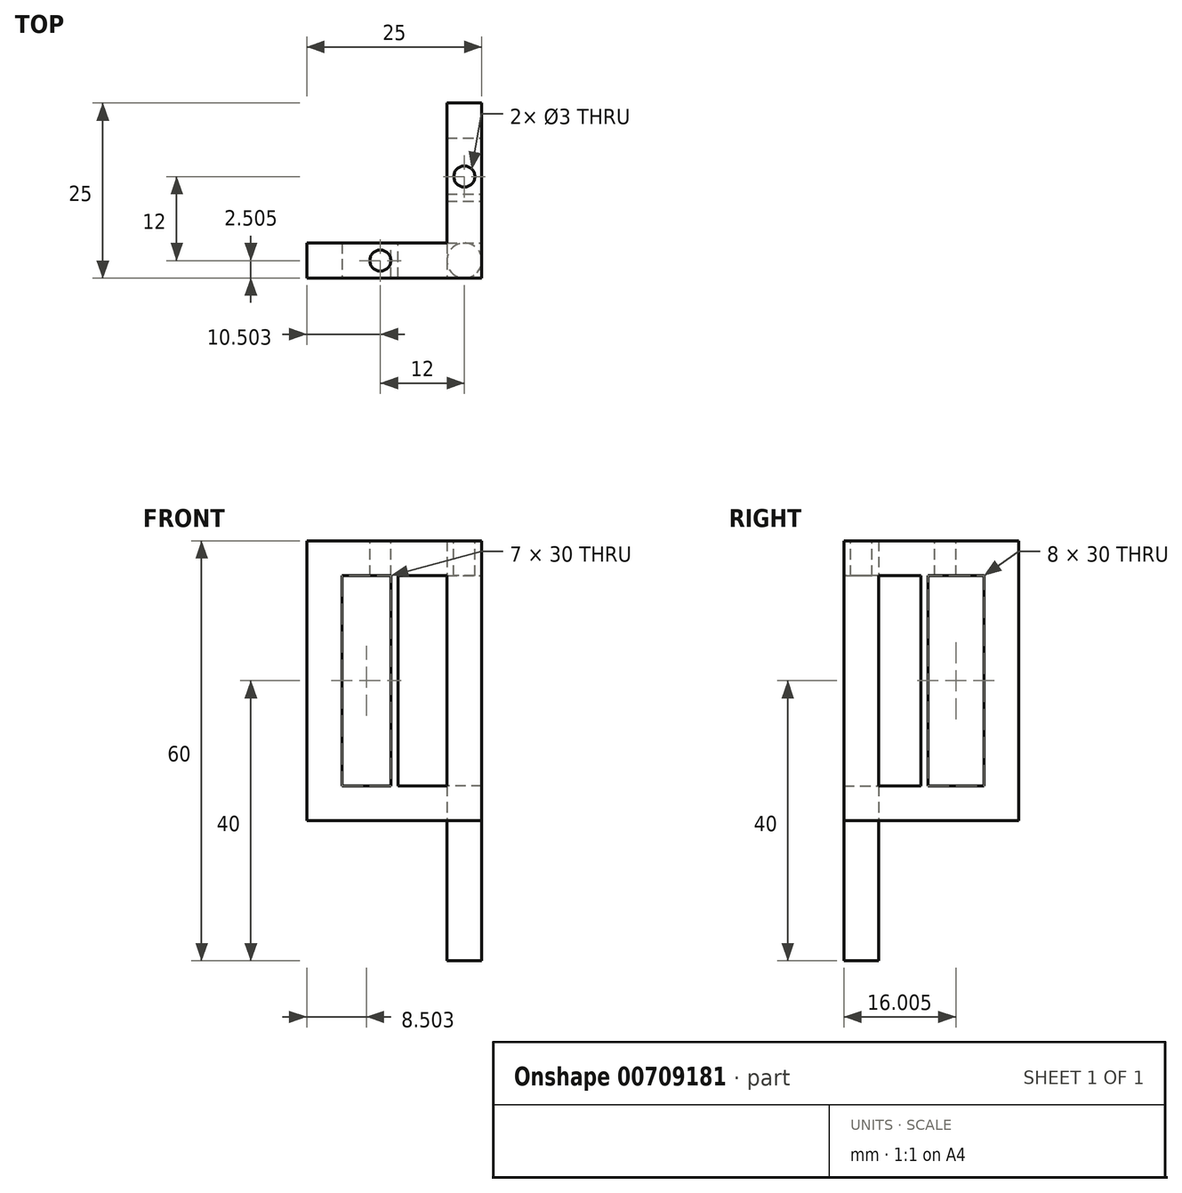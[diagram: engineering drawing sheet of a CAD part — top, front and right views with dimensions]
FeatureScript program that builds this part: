
annotation { "Feature Type Name" : "Feature", "Feature Type Description" : "" }
export const myFeature = defineFeature(function(context is Context, id is Id, definition is map)
    precondition{}
    {
        {
            var Q0;
            Q0=qCreatedBy(makeId("Top.planeOp"),FACE);
            var sketch = newSketch(context, id + "F0", { "sketchPlane" : qUnion([Q0])});
            skLineSegment(sketch, "E0.top", {"start": v(-54.93, 13.4) * mm, "end": v(-29.93, 13.4) * mm});
            skLineSegment(sketch, "E0.right", {"start": v(-29.93, 38.4) * mm, "end": v(-29.93, 13.4) * mm});
            skLineSegment(sketch, "E1.top", {"start": v(-54.93, 18.4) * mm, "end": v(-34.93, 18.4) * mm});
            skLineSegment(sketch, "E1.right", {"start": v(-34.93, 38.4) * mm, "end": v(-34.93, 18.4) * mm});
            skLineSegment(sketch, "E2", {"start": v(-49.93, 18.4) * mm, "end": v(-49.93, 13.4) * mm});
            skLineSegment(sketch, "E3", {"start": v(-34.93, 33.4) * mm, "end": v(-29.93, 33.4) * mm});
            skPoint(sketch, "E4", {"position": v(-32.43, 15.9) * mm});
            skCircle(sketch, "E5", {"center": v(-32.43, 15.9) * mm, "radius": 2.5 * mm});
            skLineSegment(sketch, "E6.bottom", {"start": v(-34.93, 18.4) * mm, "end": v(-29.93, 18.4) * mm});
            skLineSegment(sketch, "E6.top", {"start": v(-34.93, 13.4) * mm, "end": v(-29.93, 13.4) * mm});
            skLineSegment(sketch, "E6.left", {"start": v(-34.93, 18.4) * mm, "end": v(-34.93, 13.4) * mm});
            skLineSegment(sketch, "E6.right", {"start": v(-29.93, 18.4) * mm, "end": v(-29.93, 13.4) * mm});
            skLineSegment(sketch, "E7", {"start": v(-34.93, 38.4) * mm, "end": v(-29.93, 38.4) * mm});
            skLineSegment(sketch, "E8", {"start": v(-54.93, 18.4) * mm, "end": v(-54.93, 13.4) * mm});
            skLineSegment(sketch, "E9.bottom", {"start": v(-34.93, 24.4) * mm, "end": v(-29.93, 24.4) * mm});
            skLineSegment(sketch, "E9.top", {"start": v(-34.93, 25.4) * mm, "end": v(-29.93, 25.4) * mm});
            skLineSegment(sketch, "E9.left", {"start": v(-34.93, 24.4) * mm, "end": v(-34.93, 25.4) * mm});
            skLineSegment(sketch, "E9.right", {"start": v(-29.93, 24.4) * mm, "end": v(-29.93, 25.4) * mm});
            skLineSegment(sketch, "E10.bottom", {"start": v(-42.93, 13.4) * mm, "end": v(-41.93, 13.4) * mm});
            skLineSegment(sketch, "E10.top", {"start": v(-42.93, 18.4) * mm, "end": v(-41.93, 18.4) * mm});
            skLineSegment(sketch, "E10.left", {"start": v(-41.93, 13.4) * mm, "end": v(-41.93, 18.4) * mm});
            skLineSegment(sketch, "E10.right", {"start": v(-42.93, 13.4) * mm, "end": v(-42.93, 18.4) * mm});
            skSolve(sketch);
        }
        {
            var Q0;
            {var subQ0=sQuery(id+"F0.wireOp",EDGE,"E3");Q0=makeQuery(id+"F0.imprint","IMPRINT",FACE,{"disambiguationData":[TD([[makeQuery(id+"F0.imprint","IMPRINT",EDGE,{"derivedFrom":subQ0}),-1.0]])]});}
            var Q1;
            {var subQ0=sQuery(id+"F0.wireOp",EDGE,"E2");Q1=makeQuery(id+"F0.imprint","IMPRINT",FACE,{"disambiguationData":[TD([[makeQuery(id+"F0.imprint","IMPRINT",EDGE,{"derivedFrom":subQ0}),1.0]])]});}
            var Q2;
            {var subQ0=sQuery(id+"F0.wireOp",EDGE,"E2");Q2=makeQuery(id+"F0.imprint","IMPRINT",FACE,{"disambiguationData":[TD([[makeQuery(id+"F0.imprint","IMPRINT",EDGE,{"derivedFrom":subQ0}),-1.0]])]});}
            var Q3;
            {var subQ0=sQuery(id+"F0.wireOp",EDGE,"E3");Q3=makeQuery(id+"F0.imprint","IMPRINT",FACE,{"disambiguationData":[TD([[makeQuery(id+"F0.imprint","IMPRINT",EDGE,{"derivedFrom":subQ0}),1.0]])]});}
            var Q4;
            {var subQ0=sQuery(id+"F0.wireOp",EDGE,"E5");var subQ1=makeQuery(id+"F0.imprint","INTERSECT",VERTEX,{"derivedFrom":[subQ0,sQuery(id+"F0.wireOp",EDGE,"E6.bottom")]});Q4=makeQuery(id+"F0.imprint","IMPRINT",FACE,{"disambiguationData":[TD([[makeQuery(id+"F0.imprint","IMPRINT",EDGE,{"disambiguationData":[TD([[subQ1,1.0]])],"derivedFrom":subQ0}),1.0]])]});}
            var Q5;
            {var subQ0=sQuery(id+"F0.wireOp",EDGE,"E6.bottom");var subQ1=sQuery(id+"F0.wireOp",EDGE,"E0.right");var subQ2=makeQuery(id+"F0.imprint","INTERSECT",VERTEX,{"derivedFrom":[subQ1,subQ0]});Q5=makeQuery(id+"F0.imprint","IMPRINT",FACE,{"disambiguationData":[TD([[makeQuery(id+"F0.imprint","IMPRINT",EDGE,{"disambiguationData":[TD([[subQ2,-1.0]])],"derivedFrom":subQ1}),-1.0]])]});}
            var Q6;
            {var subQ0=sQuery(id+"F0.wireOp",EDGE,"E6.left");var subQ1=sQuery(id+"F0.wireOp",EDGE,"E0.top");var subQ2=makeQuery(id+"F0.imprint","INTERSECT",VERTEX,{"derivedFrom":[subQ1,subQ0]});Q6=makeQuery(id+"F0.imprint","IMPRINT",FACE,{"disambiguationData":[TD([[makeQuery(id+"F0.imprint","IMPRINT",EDGE,{"disambiguationData":[TD([[subQ2,-1.0]])],"derivedFrom":subQ1}),1.0]])]});}
            var Q7;
            {var subQ0=sQuery(id+"F0.wireOp",EDGE,"E0.right");var subQ1=sQuery(id+"F0.wireOp",EDGE,"E0.top");var subQ2=makeQuery(id+"F0.imprint","INTERSECT",VERTEX,{"derivedFrom":[subQ1,subQ0]});Q7=makeQuery(id+"F0.imprint","IMPRINT",FACE,{"disambiguationData":[TD([[makeQuery(id+"F0.imprint","IMPRINT",EDGE,{"disambiguationData":[TD([[subQ2,1.0]])],"derivedFrom":subQ1}),1.0]])]});}
            var Q8;
            {var subQ0=sQuery(id+"F0.wireOp",EDGE,"E6.bottom");var subQ1=sQuery(id+"F0.wireOp",EDGE,"E5");var subQ2=makeQuery(id+"F0.imprint","INTERSECT",VERTEX,{"derivedFrom":[subQ1,subQ0]});Q8=makeQuery(id+"F0.imprint","IMPRINT",FACE,{"disambiguationData":[TD([[makeQuery(id+"F0.imprint","IMPRINT",EDGE,{"disambiguationData":[TD([[subQ2,-1.0]])],"derivedFrom":subQ1}),-1.0]])]});}
            var Q9;
            {var subQ6=sQuery(id+"F0.wireOp",EDGE,"E10.left");Q9=makeQuery(id+"F0.imprint","IMPRINT",FACE,{"disambiguationData":[TD([[makeQuery(id+"F0.imprint","IMPRINT",EDGE,{"derivedFrom":subQ6}),-1.0]])]});}
            var Q10;
            {var subQ0=sQuery(id+"F0.wireOp",EDGE,"E10.left");Q10=makeQuery(id+"F0.imprint","IMPRINT",FACE,{"disambiguationData":[TD([[makeQuery(id+"F0.imprint","IMPRINT",EDGE,{"derivedFrom":subQ0}),1.0]])]});}
            var Q11;
            {var subQ6=sQuery(id+"F0.wireOp",EDGE,"E9.bottom");Q11=makeQuery(id+"F0.imprint","IMPRINT",FACE,{"disambiguationData":[TD([[makeQuery(id+"F0.imprint","IMPRINT",EDGE,{"derivedFrom":subQ6}),-1.0]])]});}
            var Q12;
            {var subQ0=sQuery(id+"F0.wireOp",EDGE,"E9.bottom");Q12=makeQuery(id+"F0.imprint","IMPRINT",FACE,{"disambiguationData":[TD([[makeQuery(id+"F0.imprint","IMPRINT",EDGE,{"derivedFrom":subQ0}),1.0]])]});}
            extrude(context, id + "F1", {"entities" : qUnion([Q0, Q1, Q2, Q3, Q4, Q5, Q6, Q7, Q8, Q9, Q10, Q11, Q12]), "depth" : 5 * mm, "offsetDistance" : 25 * mm});
        }
        {
            var Q0;
            {var subQ0=sQuery(id+"F0.wireOp",EDGE,"E2");Q0=makeQuery(id+"F0.imprint","IMPRINT",FACE,{"disambiguationData":[TD([[makeQuery(id+"F0.imprint","IMPRINT",EDGE,{"derivedFrom":subQ0}),-1.0]])]});}
            var Q1;
            {var subQ0=sQuery(id+"F0.wireOp",EDGE,"E6.bottom");var subQ1=sQuery(id+"F0.wireOp",EDGE,"E5");var subQ2=makeQuery(id+"F0.imprint","INTERSECT",VERTEX,{"derivedFrom":[subQ1,subQ0]});Q1=makeQuery(id+"F0.imprint","IMPRINT",FACE,{"disambiguationData":[TD([[makeQuery(id+"F0.imprint","IMPRINT",EDGE,{"disambiguationData":[TD([[subQ2,-1.0]])],"derivedFrom":subQ1}),-1.0]])]});}
            var Q2;
            {var subQ0=sQuery(id+"F0.wireOp",EDGE,"E6.left");var subQ1=sQuery(id+"F0.wireOp",EDGE,"E0.top");var subQ2=makeQuery(id+"F0.imprint","INTERSECT",VERTEX,{"derivedFrom":[subQ1,subQ0]});Q2=makeQuery(id+"F0.imprint","IMPRINT",FACE,{"disambiguationData":[TD([[makeQuery(id+"F0.imprint","IMPRINT",EDGE,{"disambiguationData":[TD([[subQ2,-1.0]])],"derivedFrom":subQ1}),1.0]])]});}
            var Q3;
            {var subQ0=sQuery(id+"F0.wireOp",EDGE,"E5");var subQ1=makeQuery(id+"F0.imprint","INTERSECT",VERTEX,{"derivedFrom":[subQ0,sQuery(id+"F0.wireOp",EDGE,"E6.bottom")]});Q3=makeQuery(id+"F0.imprint","IMPRINT",FACE,{"disambiguationData":[TD([[makeQuery(id+"F0.imprint","IMPRINT",EDGE,{"disambiguationData":[TD([[subQ1,1.0]])],"derivedFrom":subQ0}),1.0]])]});}
            var Q4;
            {var subQ0=sQuery(id+"F0.wireOp",EDGE,"E6.bottom");var subQ1=sQuery(id+"F0.wireOp",EDGE,"E0.right");var subQ2=makeQuery(id+"F0.imprint","INTERSECT",VERTEX,{"derivedFrom":[subQ1,subQ0]});Q4=makeQuery(id+"F0.imprint","IMPRINT",FACE,{"disambiguationData":[TD([[makeQuery(id+"F0.imprint","IMPRINT",EDGE,{"disambiguationData":[TD([[subQ2,-1.0]])],"derivedFrom":subQ1}),-1.0]])]});}
            var Q5;
            {var subQ0=sQuery(id+"F0.wireOp",EDGE,"E0.right");var subQ1=sQuery(id+"F0.wireOp",EDGE,"E0.top");var subQ2=makeQuery(id+"F0.imprint","INTERSECT",VERTEX,{"derivedFrom":[subQ1,subQ0]});Q5=makeQuery(id+"F0.imprint","IMPRINT",FACE,{"disambiguationData":[TD([[makeQuery(id+"F0.imprint","IMPRINT",EDGE,{"disambiguationData":[TD([[subQ2,1.0]])],"derivedFrom":subQ1}),1.0]])]});}
            var Q6;
            {var subQ0=sQuery(id+"F0.wireOp",EDGE,"E3");Q6=makeQuery(id+"F0.imprint","IMPRINT",FACE,{"disambiguationData":[TD([[makeQuery(id+"F0.imprint","IMPRINT",EDGE,{"derivedFrom":subQ0}),1.0]])]});}
            var Q7;
            {var subQ0=sQuery(id+"F0.wireOp",EDGE,"E10.left");Q7=makeQuery(id+"F0.imprint","IMPRINT",FACE,{"disambiguationData":[TD([[makeQuery(id+"F0.imprint","IMPRINT",EDGE,{"derivedFrom":subQ0}),1.0]])]});}
            var Q8;
            {var subQ0=sQuery(id+"F0.wireOp",EDGE,"E9.bottom");Q8=makeQuery(id+"F0.imprint","IMPRINT",FACE,{"disambiguationData":[TD([[makeQuery(id+"F0.imprint","IMPRINT",EDGE,{"derivedFrom":subQ0}),1.0]])]});}
            extrude(context, id + "F2", {"entities" : qUnion([Q0, Q1, Q2, Q3, Q4, Q5, Q6, Q7, Q8]), "operationType" : NewBodyOperationType.ADD, "depth" : 40 * mm, "offsetDistance" : 25 * mm});
        }
        {
            var Q0;
            {var subQ0=sQuery(id+"F0.wireOp",EDGE,"E3");Q0=makeQuery(id+"F0.imprint","IMPRINT",FACE,{"disambiguationData":[TD([[makeQuery(id+"F0.imprint","IMPRINT",EDGE,{"derivedFrom":subQ0}),-1.0]])]});}
            var Q1;
            {var subQ0=sQuery(id+"F0.wireOp",EDGE,"E2");Q1=makeQuery(id+"F0.imprint","IMPRINT",FACE,{"disambiguationData":[TD([[makeQuery(id+"F0.imprint","IMPRINT",EDGE,{"derivedFrom":subQ0}),1.0]])]});}
            var Q2;
            {var subQ6=sQuery(id+"F0.wireOp",EDGE,"E10.left");Q2=makeQuery(id+"F0.imprint","IMPRINT",FACE,{"disambiguationData":[TD([[makeQuery(id+"F0.imprint","IMPRINT",EDGE,{"derivedFrom":subQ6}),-1.0]])]});}
            var Q3;
            {var subQ6=sQuery(id+"F0.wireOp",EDGE,"E9.bottom");Q3=makeQuery(id+"F0.imprint","IMPRINT",FACE,{"disambiguationData":[TD([[makeQuery(id+"F0.imprint","IMPRINT",EDGE,{"derivedFrom":subQ6}),-1.0]])]});}
            extrude(context, id + "F3", {"entities" : qUnion([Q0, Q1, Q2, Q3]), "operationType" : NewBodyOperationType.ADD, "depth" : 40 * mm, "offsetDistance" : 25 * mm, "hasSecondDirection" : true, "secondDirectionOppositeDirection" : false, "secondDirectionDepth" : 35 * mm});
        }
        {
            var Q0;
            {var subQ0=sQuery(id+"F0.wireOp",EDGE,"E5");var subQ1=makeQuery(id+"F0.imprint","INTERSECT",VERTEX,{"derivedFrom":[subQ0,sQuery(id+"F0.wireOp",EDGE,"E6.bottom")]});Q0=makeQuery(id+"F0.imprint","IMPRINT",FACE,{"disambiguationData":[TD([[makeQuery(id+"F0.imprint","IMPRINT",EDGE,{"disambiguationData":[TD([[subQ1,1.0]])],"derivedFrom":subQ0}),1.0]])]});}
            extrude(context, id + "F4", {"entities" : qUnion([Q0]), "operationType" : NewBodyOperationType.ADD, "oppositeDirection" : true, "depth" : 20 * mm, "offsetDistance" : 25 * mm});
        }
        {
            var Q0;
            {var subQ0=sQuery(id+"F0.wireOp",EDGE,"E9.bottom");var subQ1=sQuery(id+"F0.wireOp",EDGE,"E6.bottom");var subQ2=sQuery(id+"F0.wireOp",EDGE,"E1.right");var subQ3=sQuery(id+"F0.wireOp",EDGE,"E0.right");var subQ4=sQuery(id+"F0.wireOp",EDGE,"E9.top");var subQ5=sQuery(id+"F0.wireOp",EDGE,"E3");var subQ6=sQuery(id+"F0.wireOp",EDGE,"E10.left");var subQ7=sQuery(id+"F0.wireOp",EDGE,"E6.left");var subQ8=sQuery(id+"F0.wireOp",EDGE,"E1.top");var subQ9=sQuery(id+"F0.wireOp",EDGE,"E0.top");var subQ10=sQuery(id+"F0.wireOp",EDGE,"E10.right");var subQ11=sQuery(id+"F0.wireOp",EDGE,"E2");Q0=makeQuery(id+"F3.boolean.opBoolean","MERGE",FACE,{"derivedFrom":[makeQuery(id+"F2.opExtrude","CAP_FACE",FACE,{"disambiguationData":[OSD([subQ9,subQ8,subQ11,sQuery(id+"F0.wireOp",EDGE,"E8")])],"isStart":false}),makeQuery(id+"F2.opExtrude","CAP_FACE",FACE,{"disambiguationData":[OSD([subQ9,subQ3,subQ1,subQ7])],"isStart":false}),makeQuery(id+"F2.opExtrude","CAP_FACE",FACE,{"disambiguationData":[OSD([subQ9,subQ8,subQ6,subQ10])],"isStart":false}),makeQuery(id+"F2.opExtrude","CAP_FACE",FACE,{"disambiguationData":[OSD([subQ3,subQ2,subQ5,sQuery(id+"F0.wireOp",EDGE,"E7")])],"isStart":false}),makeQuery(id+"F2.opExtrude","CAP_FACE",FACE,{"disambiguationData":[OSD([subQ3,subQ2,subQ0,subQ4])],"isStart":false}),makeQuery(id+"F3.opExtrude","CAP_FACE",FACE,{"disambiguationData":[OSD([subQ9,subQ8,subQ11,subQ10])],"isStart":false}),makeQuery(id+"F3.opExtrude","CAP_FACE",FACE,{"disambiguationData":[OSD([subQ9,subQ8,subQ7,subQ6])],"isStart":false}),makeQuery(id+"F3.opExtrude","CAP_FACE",FACE,{"disambiguationData":[OSD([subQ3,subQ2,subQ5,subQ4])],"isStart":false}),makeQuery(id+"F3.opExtrude","CAP_FACE",FACE,{"disambiguationData":[OSD([subQ3,subQ2,subQ1,subQ0])],"isStart":false})]});}
            var sketch = newSketch(context, id + "F5", { "sketchPlane" : qUnion([Q0])});
            skPoint(sketch, "E11", {"position": v(-32.43, 15.9) * mm});
            skPoint(sketch, "E12", {"position": v(-44.43, 15.9) * mm});
            skPoint(sketch, "E13", {"position": v(-32.43, 27.9) * mm});
            skSolve(sketch);
        }
        {
            var Q0;
            Q0=sQuery(id+"F5.wireOp",VERTEX,"E12");
            var Q1;
            Q1=sQuery(id+"F5.wireOp",VERTEX,"E13");
            var Q2;
            Q2=makeQuery(id+"F1.opExtrude","SWEPT_BODY",BODY,{"disambiguationData":[OSD([sQuery(id+"F0.wireOp",EDGE,"E0.top"),sQuery(id+"F0.wireOp",EDGE,"E0.right"),sQuery(id+"F0.wireOp",EDGE,"E1.top"),sQuery(id+"F0.wireOp",EDGE,"E1.right"),sQuery(id+"F0.wireOp",EDGE,"E7"),sQuery(id+"F0.wireOp",EDGE,"E8")])]});
            hole(context, id + "F6", {"style" : HoleStyle.SIMPLE, "endStyle" : HoleEndStyle.BLIND, "holeDiameter" : 3 * mm, "majorDiameter" : 5 * mm, "holeDepth" : 20 * mm, "isTappedThrough" : true, "tappedDepth" : 12 * mm, "tapClearance" : 3, "locations" : qUnion([Q0, Q1]), "scope" : qUnion([Q2])});
        }
    });
